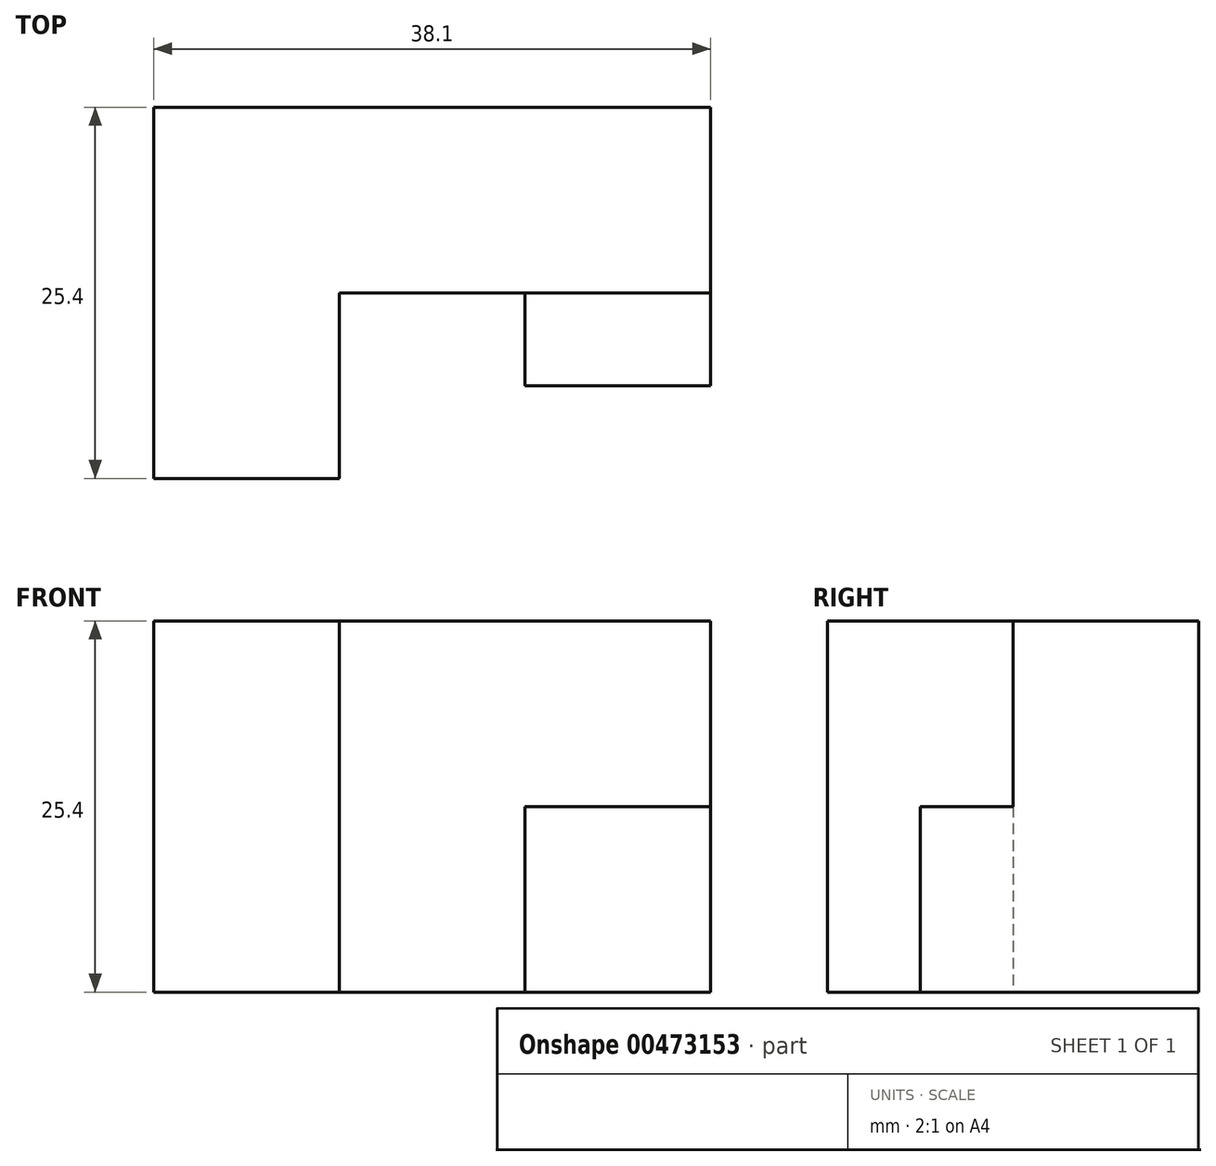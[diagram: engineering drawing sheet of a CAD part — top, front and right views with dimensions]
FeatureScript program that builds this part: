
annotation { "Feature Type Name" : "Feature", "Feature Type Description" : "" }
export const myFeature = defineFeature(function(context is Context, id is Id, definition is map)
    precondition{}
    {
        {
            var Q0;
            Q0=qCreatedBy(makeId("Front.planeOp"),FACE);
            var sketch = newSketch(context, id + "F0", { "sketchPlane" : qUnion([Q0])});
            skLineSegment(sketch, "E0.bottom", {"start": v(19.05, -12.7) * mm, "end": v(-19.05, -12.7) * mm});
            skLineSegment(sketch, "E0.top", {"start": v(19.05, 12.7) * mm, "end": v(-19.05, 12.7) * mm});
            skLineSegment(sketch, "E0.left", {"start": v(19.05, -12.7) * mm, "end": v(19.05, 12.7) * mm});
            skLineSegment(sketch, "E0.right", {"start": v(-19.05, -12.7) * mm, "end": v(-19.05, 12.7) * mm});
            skPoint(sketch, "E0.middle", {"position": v(0, 0) * mm});
            skLineSegment(sketch, "E1", {"start": v(-6.35, 12.7) * mm, "end": v(-6.35, -12.7) * mm});
            skLineSegment(sketch, "E2", {"start": v(6.35, -12.7) * mm, "end": v(6.35, 0) * mm});
            skLineSegment(sketch, "E3", {"start": v(6.35, 0) * mm, "end": v(19.05, 0) * mm});
            skSolve(sketch);
        }
        {
            var Q0;
            {var subQ0=sQuery(id+"F0.wireOp",EDGE,"E0.right");Q0=makeQuery(id+"F0.imprint","IMPRINT",FACE,{"disambiguationData":[TD([[makeQuery(id+"F0.imprint","IMPRINT",EDGE,{"derivedFrom":subQ0}),-1.0]])]});}
            extrude(context, id + "F1", {"entities" : qUnion([Q0]), "depth" : 25.4 * mm});
        }
        {
            var Q0;
            {var subQ0=sQuery(id+"F0.wireOp",EDGE,"E1");Q0=makeQuery(id+"F0.imprint","IMPRINT",FACE,{"disambiguationData":[TD([[makeQuery(id+"F0.imprint","IMPRINT",EDGE,{"derivedFrom":subQ0}),1.0]])]});}
            extrude(context, id + "F2", {"entities" : qUnion([Q0]), "operationType" : NewBodyOperationType.ADD, "depth" : 12.7 * mm});
        }
        {
            var Q0;
            {var subQ3=sQuery(id+"F0.wireOp",EDGE,"E2");Q0=makeQuery(id+"F0.imprint","IMPRINT",FACE,{"disambiguationData":[TD([[makeQuery(id+"F0.imprint","IMPRINT",EDGE,{"derivedFrom":subQ3}),-1.0]])]});}
            extrude(context, id + "F3", {"entities" : qUnion([Q0]), "operationType" : NewBodyOperationType.ADD, "depth" : 19.05 * mm});
        }
    });
